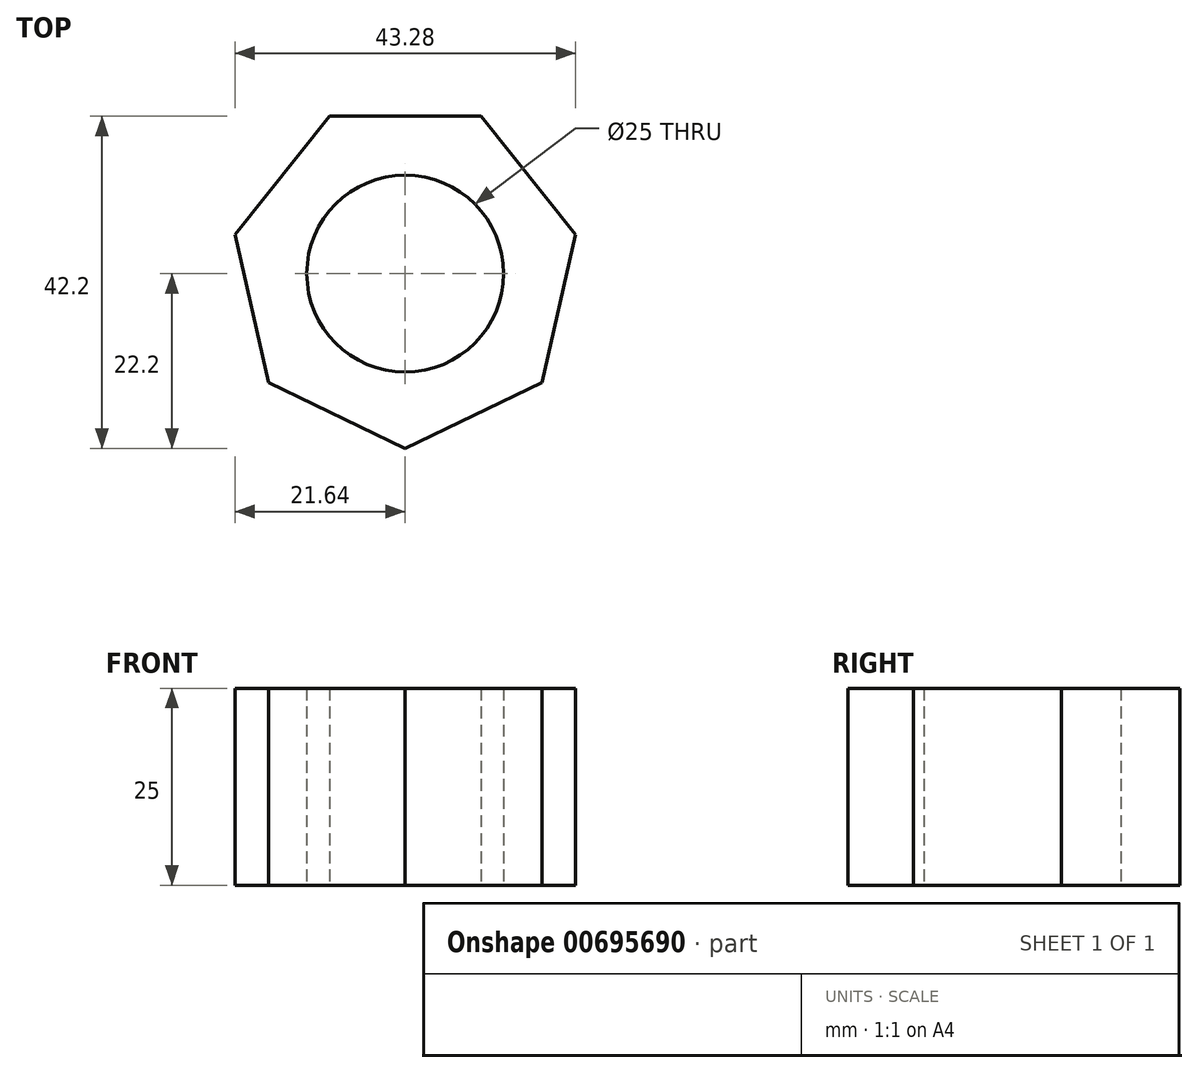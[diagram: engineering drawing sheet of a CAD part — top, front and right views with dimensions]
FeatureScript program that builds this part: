
annotation { "Feature Type Name" : "Feature", "Feature Type Description" : "" }
export const myFeature = defineFeature(function(context is Context, id is Id, definition is map)
    precondition{}
    {
        {
            var Q0;
            Q0=qCreatedBy(makeId("Top.planeOp"),FACE);
            var sketch = newSketch(context, id + "F0", { "sketchPlane" : qUnion([Q0])});
            skCircle(sketch, "E0", {"center": v(0, 0) * mm, "radius": 20 * mm});
            skCircle(sketch, "E1", {"center": v(0, 0) * mm, "radius": 12.5 * mm});
            skCircle(sketch, "E2.cCircle", {"center": v(0, 0) * mm, "radius": 20 * mm, "construction": true});
            skLineSegment(sketch, "E2.0", {"start": v(-9.63, 20) * mm, "end": v(9.63, 20) * mm});
            skLineSegment(sketch, "E2.1", {"start": v(9.63, 20) * mm, "end": v(21.64, 4.94) * mm});
            skLineSegment(sketch, "E2.2", {"start": v(21.64, 4.94) * mm, "end": v(17.36, -13.84) * mm});
            skLineSegment(sketch, "E2.3", {"start": v(17.36, -13.84) * mm, "end": v(0, -22.2) * mm});
            skLineSegment(sketch, "E2.4", {"start": v(0, -22.2) * mm, "end": v(-17.36, -13.84) * mm});
            skLineSegment(sketch, "E2.5", {"start": v(-17.36, -13.84) * mm, "end": v(-21.64, 4.94) * mm});
            skLineSegment(sketch, "E2.6", {"start": v(-21.64, 4.94) * mm, "end": v(-9.63, 20) * mm});
            skPoint(sketch, "E2.0.midPoint", {"position": v(0, 20) * mm});
            skSolve(sketch);
        }
        {
            var Q0;
            Q0 = qSketchRegion(id + "F0", true);
            extrude(context, id + "F1", {"entities" : qUnion([Q0]), "depth" : 25 * mm, "offsetDistance" : 25 * mm});
        }
    });
